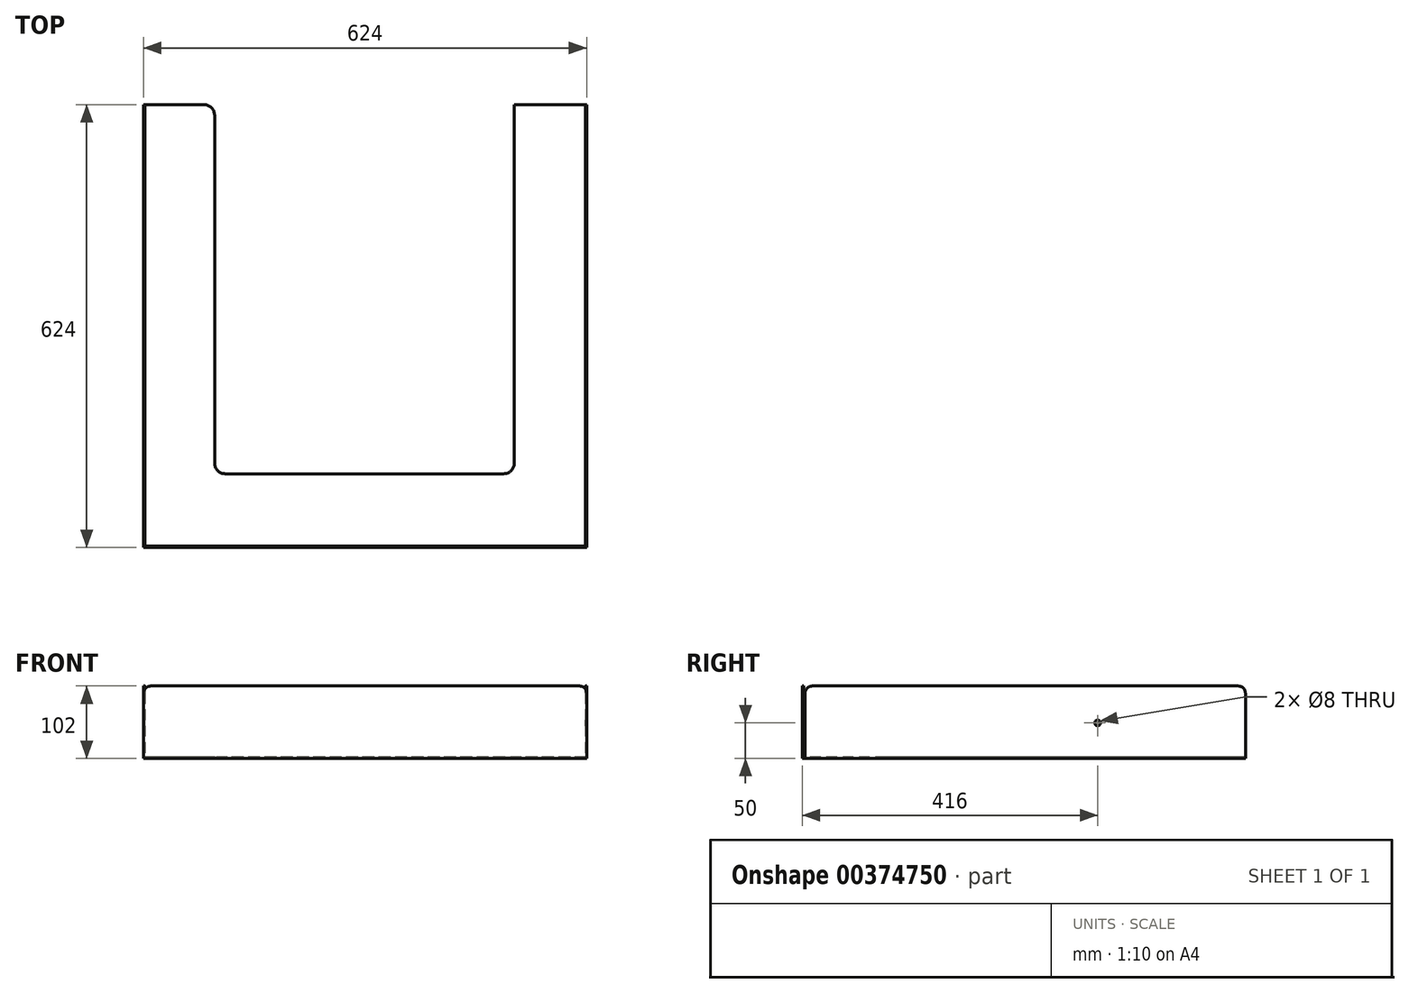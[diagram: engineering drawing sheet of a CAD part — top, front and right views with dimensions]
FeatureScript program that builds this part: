
annotation { "Feature Type Name" : "Feature", "Feature Type Description" : "" }
export const myFeature = defineFeature(function(context is Context, id is Id, definition is map)
    precondition{}
    {
        {
            var Q0;
            Q0=qCreatedBy(makeId("Top.planeOp"),FACE);
            var sketch = newSketch(context, id + "F0", { "sketchPlane" : qUnion([Q0])});
            skLineSegment(sketch, "E0.bottom", {"start": v(312, 312) * mm, "end": v(-312, 312) * mm});
            skLineSegment(sketch, "E0.top", {"start": v(312, -312) * mm, "end": v(-312, -312) * mm});
            skLineSegment(sketch, "E0.left", {"start": v(312, 312) * mm, "end": v(312, -312) * mm});
            skLineSegment(sketch, "E0.right", {"start": v(-312, 312) * mm, "end": v(-312, -312) * mm});
            skPoint(sketch, "E0.middle", {"position": v(0, 0) * mm});
            skSolve(sketch);
        }
        {
            var Q0;
            Q0=makeQuery(id+"F0.imprint","IMPRINT",FACE,{"disambiguationData":[TD([[makeQuery(id+"F0.imprint","IMPRINT",EDGE,{"derivedFrom":sQuery(id+"F0.wireOp",EDGE,"E0.bottom")}),1.0]])]});
            extrude(context, id + "F1", {"entities" : qUnion([Q0]), "depth" : 2 * mm});
        }
        {
            var Q0;
            Q0=makeQuery(id+"F1.opExtrude","CAP_FACE",FACE,{"disambiguationData":[OSD([sQuery(id+"F0.wireOp",EDGE,"E0.bottom"),sQuery(id+"F0.wireOp",EDGE,"E0.top"),sQuery(id+"F0.wireOp",EDGE,"E0.left"),sQuery(id+"F0.wireOp",EDGE,"E0.right")])],"isStart":false});
            var sketch = newSketch(context, id + "F2", { "sketchPlane" : qUnion([Q0])});
            skLineSegment(sketch, "E1.bottom", {"start": v(-312, 312) * mm, "end": v(-310, 312) * mm});
            skLineSegment(sketch, "E1.top", {"start": v(-312, -308) * mm, "end": v(-310, -308) * mm});
            skLineSegment(sketch, "E1.left", {"start": v(-312, 312) * mm, "end": v(-312, -308) * mm});
            skLineSegment(sketch, "E1.right", {"start": v(-310, 312) * mm, "end": v(-310, -308) * mm});
            skLineSegment(sketch, "E2.bottom", {"start": v(312, 312) * mm, "end": v(310, 312) * mm});
            skLineSegment(sketch, "E2.top", {"start": v(312, -308) * mm, "end": v(310, -308) * mm});
            skLineSegment(sketch, "E2.left", {"start": v(312, 312) * mm, "end": v(312, -308) * mm});
            skLineSegment(sketch, "E2.right", {"start": v(310, 312) * mm, "end": v(310, -308) * mm});
            skLineSegment(sketch, "E3.bottom", {"start": v(312, -312) * mm, "end": v(-312, -312) * mm});
            skLineSegment(sketch, "E3.top", {"start": v(312, -310) * mm, "end": v(-312, -310) * mm});
            skLineSegment(sketch, "E3.left", {"start": v(312, -312) * mm, "end": v(312, -310) * mm});
            skLineSegment(sketch, "E3.right", {"start": v(-312, -312) * mm, "end": v(-312, -310) * mm});
            skSolve(sketch);
        }
        {
            var Q0;
            Q0=makeQuery(id+"F2.imprint","IMPRINT",FACE,{"disambiguationData":[TD([[makeQuery(id+"F2.imprint","IMPRINT",EDGE,{"derivedFrom":sQuery(id+"F2.wireOp",EDGE,"E3.bottom")}),-1.0]])]});
            var Q1;
            Q1=makeQuery(id+"F2.imprint","IMPRINT",FACE,{"disambiguationData":[TD([[makeQuery(id+"F2.imprint","IMPRINT",EDGE,{"derivedFrom":sQuery(id+"F2.wireOp",EDGE,"E1.bottom")}),1.0]])]});
            var Q2;
            Q2=makeQuery(id+"F2.imprint","IMPRINT",FACE,{"disambiguationData":[TD([[makeQuery(id+"F2.imprint","IMPRINT",EDGE,{"derivedFrom":sQuery(id+"F2.wireOp",EDGE,"E2.bottom")}),1.0]])]});
            extrude(context, id + "F3", {"entities" : qUnion([Q0, Q1, Q2]), "operationType" : NewBodyOperationType.ADD, "depth" : 100 * mm});
        }
        {
            var Q0;
            Q0=makeQuery(id+"F3.opExtrude","CAP_EDGE",EDGE,{"disambiguationData":[OSD([sQuery(id+"F2.wireOp",EDGE,"E2.bottom")])],"isStart":false});
            var Q1;
            Q1=makeQuery(id+"F3.opExtrude","CAP_EDGE",EDGE,{"disambiguationData":[OSD([sQuery(id+"F2.wireOp",EDGE,"E1.bottom")])],"isStart":false});
            var Q2;
            Q2=makeQuery(id+"F3.opExtrude","CAP_EDGE",EDGE,{"disambiguationData":[OSD([sQuery(id+"F2.wireOp",EDGE,"E3.right")])],"isStart":false});
            var Q3;
            Q3=makeQuery(id+"F3.opExtrude","CAP_EDGE",EDGE,{"disambiguationData":[OSD([sQuery(id+"F2.wireOp",EDGE,"E1.top")])],"isStart":false});
            var Q4;
            Q4=makeQuery(id+"F3.opExtrude","CAP_EDGE",EDGE,{"disambiguationData":[OSD([sQuery(id+"F2.wireOp",EDGE,"E2.top")])],"isStart":false});
            var Q5;
            Q5=makeQuery(id+"F3.opExtrude","CAP_EDGE",EDGE,{"disambiguationData":[OSD([sQuery(id+"F2.wireOp",EDGE,"E3.left")])],"isStart":false});
            fillet(context, id + "F4", {"entities" : qUnion([Q0, Q1, Q2, Q3, Q4, Q5]), "radius" : 10 * mm, "tangentPropagation" : true, "allowEdgeOverflow" : false});
        }
        {
            var Q0;
            Q0=makeQuery(id+"F3.boolean.opBoolean","MERGE",FACE,{"derivedFrom":[makeQuery(id+"F1.opExtrude","SWEPT_FACE",FACE,{"disambiguationData":[OSD([sQuery(id+"F0.wireOp",EDGE,"E0.right")])]}),makeQuery(id+"F3.opExtrude","SWEPT_FACE",FACE,{"disambiguationData":[OSD([sQuery(id+"F2.wireOp",EDGE,"E1.left")])]}),makeQuery(id+"F3.opExtrude","SWEPT_FACE",FACE,{"disambiguationData":[OSD([sQuery(id+"F2.wireOp",EDGE,"E3.right")])]})]});
            var sketch = newSketch(context, id + "F5", { "sketchPlane" : qUnion([Q0])});
            skCircle(sketch, "E4", {"center": v(-104, 50) * mm, "radius": 2.5 * mm});
            skPoint(sketch, "E4.centerSnap0", {"position": v(0, 0) * mm});
            skSolve(sketch);
        }
        {
            var Q0;
            Q0=sQuery(id+"F5.wireOp",VERTEX,"E4.center");
            var Q1;
            Q1=makeQuery(id+"F1.opExtrude","SWEPT_BODY",BODY,{"disambiguationData":[OSD([sQuery(id+"F0.wireOp",EDGE,"E0.bottom"),sQuery(id+"F0.wireOp",EDGE,"E0.top"),sQuery(id+"F0.wireOp",EDGE,"E0.left"),sQuery(id+"F0.wireOp",EDGE,"E0.right")])]});
            hole(context, id + "F6", {"style" : HoleStyle.SIMPLE, "endStyle" : HoleEndStyle.THROUGH, "holeDiameter" : 8 * mm, "isTappedThrough" : true, "tappedDepth" : 12 * mm, "tapClearance" : 3, "locations" : qUnion([Q0]), "scope" : qUnion([Q1])});
        }
        {
            var Q0;
            Q0=makeQuery(id+"F1.opExtrude","CAP_FACE",FACE,{"disambiguationData":[OSD([sQuery(id+"F0.wireOp",EDGE,"E0.bottom"),sQuery(id+"F0.wireOp",EDGE,"E0.top"),sQuery(id+"F0.wireOp",EDGE,"E0.left"),sQuery(id+"F0.wireOp",EDGE,"E0.right")])],"isStart":false});
            var sketch = newSketch(context, id + "F7", { "sketchPlane" : qUnion([Q0])});
            skLineSegment(sketch, "E5.bottom", {"start": v(210, 312) * mm, "end": v(-212, 312) * mm});
            skLineSegment(sketch, "E5.top", {"start": v(210, -208) * mm, "end": v(-212, -208) * mm});
            skLineSegment(sketch, "E5.left", {"start": v(210, 312) * mm, "end": v(210, -208) * mm});
            skLineSegment(sketch, "E5.right", {"start": v(-212, 312) * mm, "end": v(-212, -208) * mm});
            skSolve(sketch);
        }
        {
            var Q0;
            Q0=makeQuery(id+"F7.imprint","IMPRINT",FACE,{"disambiguationData":[TD([[makeQuery(id+"F7.imprint","IMPRINT",EDGE,{"derivedFrom":sQuery(id+"F7.wireOp",EDGE,"E5.bottom")}),1.0]])]});
            extrude(context, id + "F8", {"entities" : qUnion([Q0]), "operationType" : NewBodyOperationType.REMOVE, "oppositeDirection" : true, "depth" : 25 * mm});
        }
        {
            var Q0;
            Q0=makeQuery(id+"F8.boolean.opBoolean","COPY",EDGE,{"derivedFrom":makeQuery(id+"F8.opExtrude","SWEPT_EDGE",EDGE,{"disambiguationData":[OSD([sQuery(id+"F7.wireOp",EDGE,"E5.top"),sQuery(id+"F7.wireOp",EDGE,"E5.left")])]})});
            var Q1;
            Q1=makeQuery(id+"F8.boolean.opBoolean","COPY",EDGE,{"derivedFrom":makeQuery(id+"F8.opExtrude","SWEPT_EDGE",EDGE,{"disambiguationData":[OSD([sQuery(id+"F0.wireOp",EDGE,"E0.bottom"),sQuery(id+"F7.wireOp",EDGE,"E5.bottom"),sQuery(id+"F7.wireOp",EDGE,"E5.left")])]})});
            var Q2;
            Q2=makeQuery(id+"F8.boolean.opBoolean","COPY",EDGE,{"derivedFrom":makeQuery(id+"F8.opExtrude","SWEPT_EDGE",EDGE,{"disambiguationData":[OSD([sQuery(id+"F0.wireOp",EDGE,"E0.bottom"),sQuery(id+"F7.wireOp",EDGE,"E5.bottom"),sQuery(id+"F7.wireOp",EDGE,"E5.right")])]})});
            var Q3;
            Q3=makeQuery(id+"F8.boolean.opBoolean","COPY",EDGE,{"derivedFrom":makeQuery(id+"F8.opExtrude","SWEPT_EDGE",EDGE,{"disambiguationData":[OSD([sQuery(id+"F7.wireOp",EDGE,"E5.top"),sQuery(id+"F7.wireOp",EDGE,"E5.right")])]})});
            fillet(context, id + "F9", {"entities" : qUnion([Q0, Q1, Q2, Q3]), "radius" : 15 * mm, "tangentPropagation" : true, "allowEdgeOverflow" : false});
        }
    });
